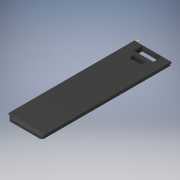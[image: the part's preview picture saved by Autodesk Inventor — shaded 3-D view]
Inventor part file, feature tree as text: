
AUTODESK INVENTOR PART (.ipt)
format: ipt  version: 2019 (Build 230136000, 136)  size: 215,040 bytes
history: native  units: mm
features: sketch x8, extrude x7, chamfer x4
ambient origin geometry x8: Origin, YZ Plane, XZ Plane, XY Plane, X Axis, Y Axis, Z Axis, Center Point
bodies: Solid1 (feature_tree)
feature tree (19):
  extrude  "Extrusion1"  Depth=3.0mm
  extrude  "Extrusion2"  Depth=2.0mm
  extrude  "Extrusion3"  Depth=6.5mm
  sketch  "Sketch4"  dims[d7=5.5mm]
  chamfer  "Chamfer1"  Distance=3.0mm
  chamfer  "Chamfer2"  Distance=4.0mm
  chamfer  "Chamfer3"  Distance=3.0mm
  extrude  "Extrusion4"  Depth=2.0mm
  extrude  "Extrusion5"  Depth=3.0mm
  extrude  "Extrusion6"  Depth=3.0mm TaperAngle=0.0deg
  extrude  "Extrusion7"  Depth=2.0mm TaperAngle=45.0deg
  chamfer  "Chamfer4"  Distance=1.0mm Angle=45.0deg
  sketch  "Sketch1"  dims[d0=22.5mm d1=3.0mm]
  sketch  "Sketch2"  dims[d2=86.75mm d3=0.0mm d4=2.0mm]
  sketch  "Sketch3"  dims[d5=90.0deg d6=6.5mm]
  sketch  "Sketch5"  dims[d8=6.5mm]
  sketch  "Sketch6"  dims[d9=5.5mm d10=3.0mm d11=0.0mm]
  sketch  "Sketch7"  dims[d12=2.5mm]
  sketch  "Sketch8"  dims[d13=90.0deg d14=4.0mm d15=3.0mm d16=4.0mm d17=3.0mm d18=3.0mm d19=0.0mm d20=1.5mm d21=2.0mm d22=45.0deg d23=1.0mm d24=2.0mm d25=45.0deg d26=0.8165mm d27=2.0mm d28=45.0deg d29=84.75mm d30=1.5mm d31=2.5mm d32=0.0mm d33=84.75mm d34=1.0mm d35=1.0mm d36=0.0mm d37=84.75mm d38=1.5mm d39=2.5mm d40=0.0mm d41=84.75mm d42=1.0mm d43=1.0mm d44=0.0mm d45=0.5mm d46=2.0mm d47=45.0deg]
